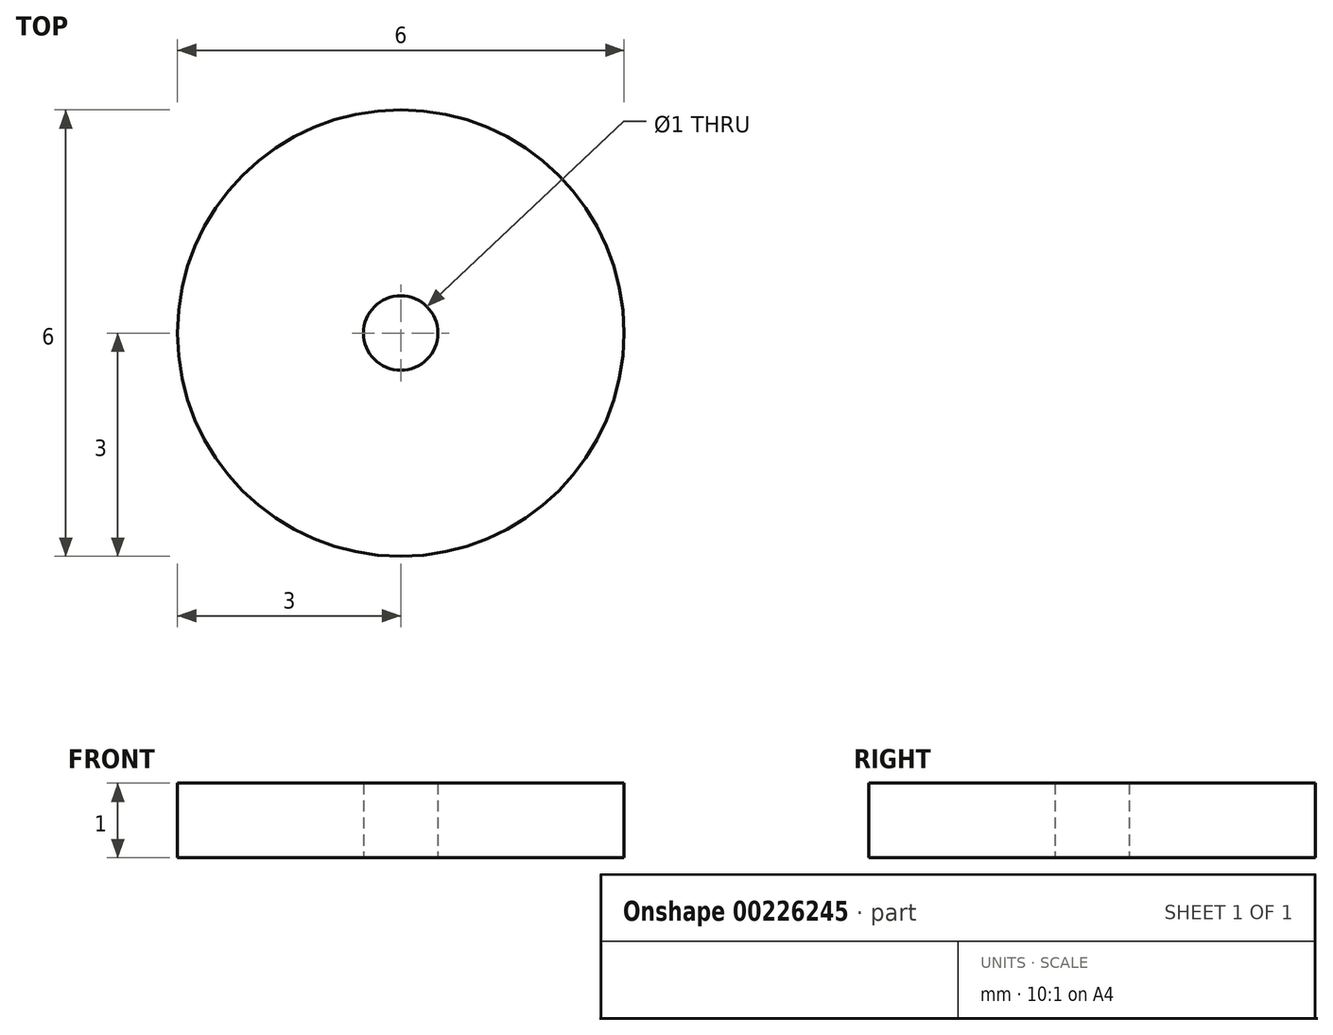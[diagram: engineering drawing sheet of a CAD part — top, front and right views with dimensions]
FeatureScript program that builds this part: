
annotation { "Feature Type Name" : "Feature", "Feature Type Description" : "" }
export const myFeature = defineFeature(function(context is Context, id is Id, definition is map)
    precondition{}
    {
        {
            var Q0;
            Q0=qCreatedBy(makeId("Top.planeOp"),FACE);
            var sketch = newSketch(context, id + "F0", { "sketchPlane" : qUnion([Q0])});
            skCircle(sketch, "E0", {"center": v(0, 0) * mm, "radius": 0.5 * mm});
            skCircle(sketch, "E1", {"center": v(0, 0) * mm, "radius": 3 * mm});
            skSolve(sketch);
        }
        {
            var Q0;
            Q0 = qSketchRegion(id + "F0", true);
            extrude(context, id + "F1", {"entities" : qUnion([Q0]), "depth" : 1 * mm});
        }
    });
